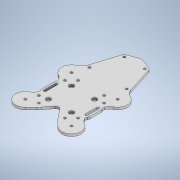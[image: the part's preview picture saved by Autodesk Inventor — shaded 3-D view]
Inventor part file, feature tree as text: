
AUTODESK INVENTOR PART (.ipt)
format: ipt  version: 2020 (Build 240168000, 168)  size: 202,240 bytes
history: native  units: in
note: dims shown in document units (in); Inventor stores cm internally (conversion verified against a paired STEP export)
features: extrude x1, sketch x1
ambient origin geometry x8: Origin, YZ Plane, XZ Plane, XY Plane, X Axis, Y Axis, Z Axis, Center Point
bodies: Solid1 (feature_tree)
feature tree (2):
  extrude  "Extrusion1"  [1 undecoded]
  sketch  "Sketch1"  dims[d0=0.1181in d1=0.0in]
note: 1 required parameter value undecoded (feature->parameter linkage not recoverable at this tier; creation-order binding heuristic only, values carry confidence <= 0.55)
